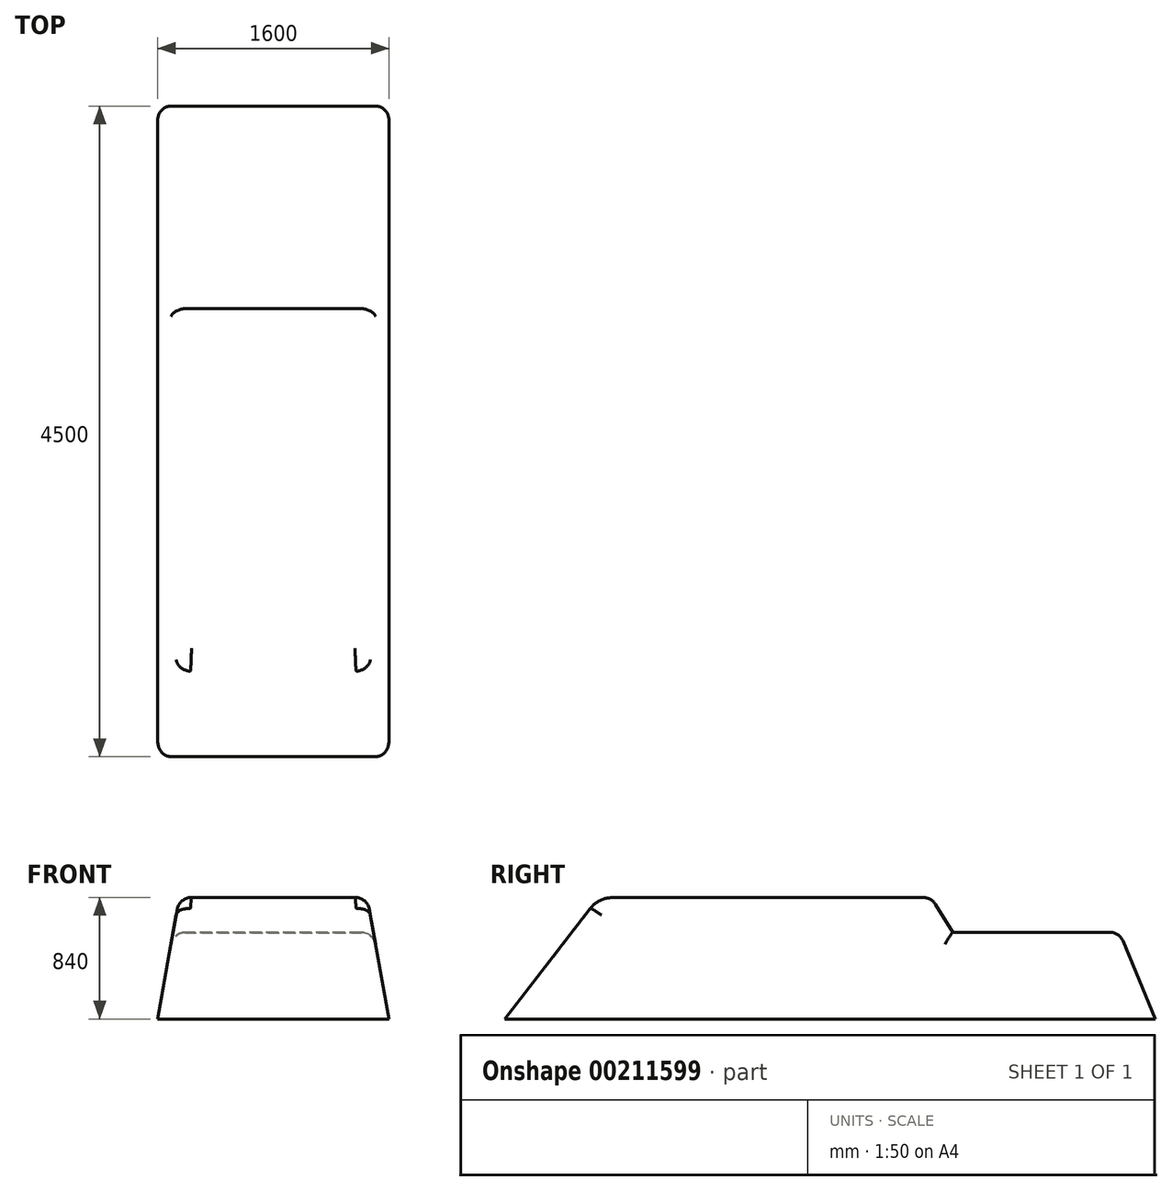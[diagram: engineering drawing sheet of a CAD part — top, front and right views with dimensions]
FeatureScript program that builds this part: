
annotation { "Feature Type Name" : "Feature", "Feature Type Description" : "" }
export const myFeature = defineFeature(function(context is Context, id is Id, definition is map)
    precondition{}
    {
        {
            var Q0;
            Q0=qCreatedBy(makeId("Right.planeOp"),FACE);
            var sketch = newSketch(context, id + "F0", { "sketchPlane" : qUnion([Q0])});
            skLineSegment(sketch, "E0", {"start": v(-1464.52, 0) * mm, "end": v(-874.57, 762.4) * mm});
            skLineSegment(sketch, "E1", {"start": v(-716.4, 840) * mm, "end": v(1430.05, 840) * mm});
            skLineSegment(sketch, "E2", {"start": v(1514.85, 793) * mm, "end": v(1635.48, 600) * mm});
            skLineSegment(sketch, "E3", {"start": v(1635.48, 600) * mm, "end": v(2718.81, 600) * mm});
            skLineSegment(sketch, "E4", {"start": v(2811.12, 538.46) * mm, "end": v(3035.48, 0) * mm});
            skLineSegment(sketch, "E5", {"start": v(3035.48, 0) * mm, "end": v(-1464.52, 0) * mm});
            skPoint(sketch, "E6.visualSharp", {"position": v(-814.52, 840) * mm});
            skArc(sketch, "E6.filletArc", {"start": v(-716.4, 840) * mm, "mid": v(-804.5, 819.55) * mm, "end": v(-874.57, 762.4) * mm});
            skPoint(sketch, "E7.visualSharp", {"position": v(1485.48, 840) * mm});
            skArc(sketch, "E7.filletArc", {"start": v(1514.85, 793) * mm, "mid": v(1478.53, 827.46) * mm, "end": v(1430.05, 840) * mm});
            skPoint(sketch, "E8.visualSharp", {"position": v(2785.48, 600) * mm});
            skArc(sketch, "E8.filletArc", {"start": v(2811.12, 538.46) * mm, "mid": v(2774.28, 583.2) * mm, "end": v(2718.81, 600) * mm});
            skSolve(sketch);
        }
        {
            var Q0;
            Q0=makeQuery(id+"F0.imprint","IMPRINT",FACE,{"disambiguationData":[TD([[makeQuery(id+"F0.imprint","IMPRINT",EDGE,{"derivedFrom":sQuery(id+"F0.wireOp",EDGE,"E0")}),-1.0]])]});
            var Q1;
            Q1 = qSketchRegion(id + "FQhckZ4ycMq1syb_1", true);
            extrude(context, id + "F1", {"entities" : qUnion([Q0, Q1]), "depth" : 800 * mm});
        }
        {
            var Q0;
            Q0=qCreatedBy(makeId("Front.planeOp"),FACE);
            var sketch = newSketch(context, id + "F2", { "sketchPlane" : qUnion([Q0])});
            skLineSegment(sketch, "E9", {"start": v(0, 0) * mm, "end": v(0, 840) * mm});
            skLineSegment(sketch, "E10", {"start": v(0, 840) * mm, "end": v(150, 840) * mm});
            skLineSegment(sketch, "E11", {"start": v(150, 840) * mm, "end": v(0, 0) * mm});
            skSolve(sketch);
        }
        {
            var Q0;
            Q0 = qSketchRegion(id + "F2", true);
            extrude(context, id + "F3", {"entities" : qUnion([Q0]), "operationType" : NewBodyOperationType.REMOVE, "oppositeDirection" : true, "depth" : 3490 * mm, "hasSecondDirection" : true, "secondDirectionOppositeDirection" : false, "secondDirectionDepth" : 1678 * mm});
        }
        {
            var Q0;
            Q0=makeQuery(id+"F3.boolean.opBoolean","INTERSECT",EDGE,{"derivedFrom":[makeQuery(id+"F1.opExtrude","SWEPT_FACE",FACE,{"disambiguationData":[OSD([sQuery(id+"F0.wireOp",EDGE,"E0")])]}),makeQuery(id+"F3.opExtrude","SWEPT_FACE",FACE,{"disambiguationData":[OSD([sQuery(id+"F2.wireOp",EDGE,"E11")])]})]});
            var Q1;
            Q1=makeQuery(id+"F3.boolean.opBoolean","COPY",EDGE,{"derivedFrom":makeQuery(id+"F3.opExtrude","SWEPT_EDGE",EDGE,{"disambiguationData":[OSD([sQuery(id+"F2.wireOp",EDGE,"E10"),sQuery(id+"F2.wireOp",EDGE,"E11")])]})});
            var Q2;
            Q2=makeQuery(id+"F3.boolean.opBoolean","INTERSECT",EDGE,{"derivedFrom":[makeQuery(id+"F1.opExtrude","SWEPT_FACE",FACE,{"disambiguationData":[OSD([sQuery(id+"F0.wireOp",EDGE,"E6.filletArc")])]}),makeQuery(id+"F3.opExtrude","SWEPT_FACE",FACE,{"disambiguationData":[OSD([sQuery(id+"F2.wireOp",EDGE,"E11")])]})]});
            var Q3;
            Q3=makeQuery(id+"F3.boolean.opBoolean","INTERSECT",EDGE,{"derivedFrom":[makeQuery(id+"F1.opExtrude","SWEPT_FACE",FACE,{"disambiguationData":[OSD([sQuery(id+"F0.wireOp",EDGE,"E2")])]}),makeQuery(id+"F3.opExtrude","SWEPT_FACE",FACE,{"disambiguationData":[OSD([sQuery(id+"F2.wireOp",EDGE,"E11")])]})]});
            var Q4;
            Q4=makeQuery(id+"F3.boolean.opBoolean","INTERSECT",EDGE,{"derivedFrom":[makeQuery(id+"F1.opExtrude","SWEPT_FACE",FACE,{"disambiguationData":[OSD([sQuery(id+"F0.wireOp",EDGE,"E7.filletArc")])]}),makeQuery(id+"F3.opExtrude","SWEPT_FACE",FACE,{"disambiguationData":[OSD([sQuery(id+"F2.wireOp",EDGE,"E11")])]})]});
            var Q5;
            Q5=makeQuery(id+"F3.boolean.opBoolean","INTERSECT",EDGE,{"derivedFrom":[makeQuery(id+"F1.opExtrude","SWEPT_FACE",FACE,{"disambiguationData":[OSD([sQuery(id+"F0.wireOp",EDGE,"E3")])]}),makeQuery(id+"F3.opExtrude","SWEPT_FACE",FACE,{"disambiguationData":[OSD([sQuery(id+"F2.wireOp",EDGE,"E11")])]})]});
            var Q6;
            Q6=makeQuery(id+"F3.boolean.opBoolean","INTERSECT",EDGE,{"derivedFrom":[makeQuery(id+"F1.opExtrude","SWEPT_FACE",FACE,{"disambiguationData":[OSD([sQuery(id+"F0.wireOp",EDGE,"E8.filletArc")])]}),makeQuery(id+"F3.opExtrude","SWEPT_FACE",FACE,{"disambiguationData":[OSD([sQuery(id+"F2.wireOp",EDGE,"E11")])]})]});
            var Q7;
            Q7=makeQuery(id+"F3.boolean.opBoolean","INTERSECT",EDGE,{"derivedFrom":[makeQuery(id+"F1.opExtrude","SWEPT_FACE",FACE,{"disambiguationData":[OSD([sQuery(id+"F0.wireOp",EDGE,"E4")])]}),makeQuery(id+"F3.opExtrude","SWEPT_FACE",FACE,{"disambiguationData":[OSD([sQuery(id+"F2.wireOp",EDGE,"E11")])]})]});
            fillet(context, id + "F4", {"entities" : qUnion([Q0, Q1, Q2, Q3, Q4, Q5, Q6, Q7]), "radius" : 100 * mm, "tangentPropagation" : true, "allowEdgeOverflow" : false});
        }
        {
            var Q0;
            Q0=makeQuery(id+"F1.opExtrude","SWEPT_BODY",BODY,{"disambiguationData":[OSD([sQuery(id+"F0.wireOp",EDGE,"E0"),sQuery(id+"F0.wireOp",EDGE,"E1"),sQuery(id+"F0.wireOp",EDGE,"E2"),sQuery(id+"F0.wireOp",EDGE,"E3"),sQuery(id+"F0.wireOp",EDGE,"E4"),sQuery(id+"F0.wireOp",EDGE,"E5"),sQuery(id+"F0.wireOp",EDGE,"E6.filletArc"),sQuery(id+"F0.wireOp",EDGE,"E7.filletArc"),sQuery(id+"F0.wireOp",EDGE,"E8.filletArc")])]});
            var Q1;
            Q1=makeQuery(id+"F1.opExtrude","CAP_FACE",FACE,{"disambiguationData":[OSD([sQuery(id+"F0.wireOp",EDGE,"E0"),sQuery(id+"F0.wireOp",EDGE,"E1"),sQuery(id+"F0.wireOp",EDGE,"E2"),sQuery(id+"F0.wireOp",EDGE,"E3"),sQuery(id+"F0.wireOp",EDGE,"E4"),sQuery(id+"F0.wireOp",EDGE,"E5"),sQuery(id+"F0.wireOp",EDGE,"E6.filletArc"),sQuery(id+"F0.wireOp",EDGE,"E7.filletArc"),sQuery(id+"F0.wireOp",EDGE,"E8.filletArc")])],"isStart":false});
            mirror(context, id + "F5", {"operationType" : NewBodyOperationType.ADD, "entities" : qUnion([Q0]), "mirrorPlane" : qUnion([Q1])});
        }
        {
            var Q0;
            {var subQ0=makeQuery(id+"F1.opExtrude","SWEPT_FACE",FACE,{"disambiguationData":[OSD([sQuery(id+"F0.wireOp",EDGE,"E5")])]});Q0=makeQuery(id+"F5.boolean.opBoolean","MERGE",FACE,{"derivedFrom":[subQ0,makeQuery(id+"F5.opPattern","COPY",FACE,{"derivedFrom":subQ0,"instanceName":"1"})]});}
            shell(context, id + "F6", {"entities" : qUnion([Q0]), "thickness" : 3 * mm});
        }
    });
